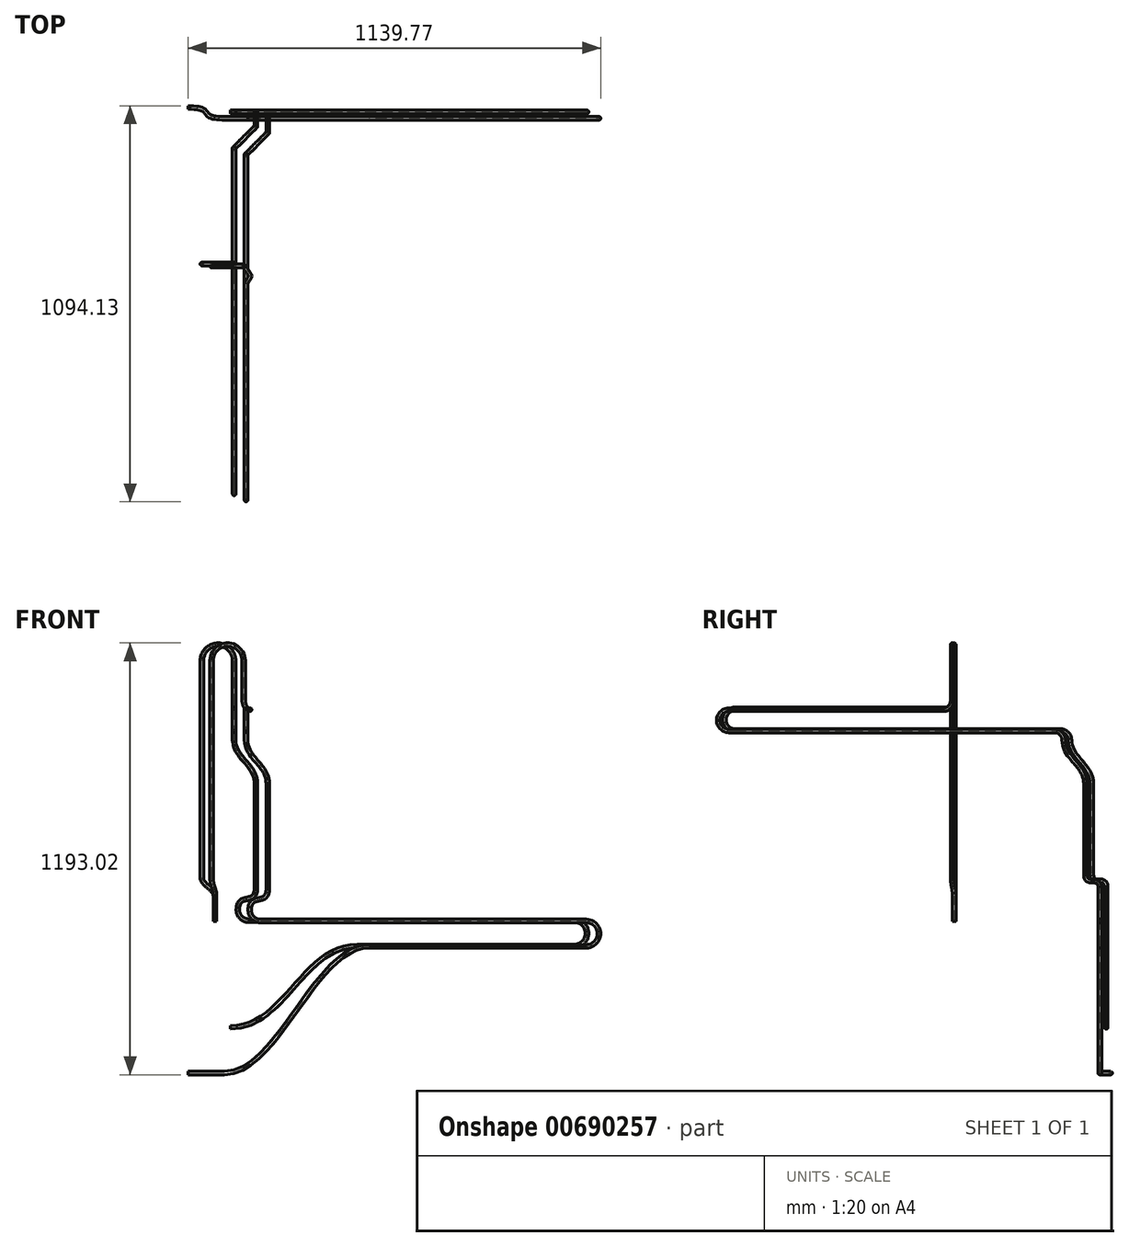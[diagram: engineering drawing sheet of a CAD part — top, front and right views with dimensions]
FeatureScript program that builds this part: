
annotation { "Feature Type Name" : "Feature", "Feature Type Description" : "" }
export const myFeature = defineFeature(function(context is Context, id is Id, definition is map)
    precondition{}
    {
        {
            var Q0;
            Q0=qCreatedBy(makeId("Top.planeOp"),FACE);
            var sketch = newSketch(context, id + "F0", { "sketchPlane" : qUnion([Q0])});
            skCircle(sketch, "E0", {"center": v(0, 0) * mm, "radius": 4.76 * mm});
            skCircle(sketch, "E1", {"center": v(0, 0) * mm, "radius": 3.17 * mm});
            skSolve(sketch);
        }
        {
            var Q0;
            Q0=qCreatedBy(makeId("Front.planeOp"),FACE);
            var sketch = newSketch(context, id + "F1", { "sketchPlane" : qUnion([Q0])});
            skLineSegment(sketch, "E2", {"start": v(0, 70) * mm, "end": v(0, 0) * mm});
            skSolve(sketch);
        }
        {
            var Q0;
            Q0=sQuery(id+"F1.wireOp",EDGE,"E2");
            cPlane(context, id + "F2", {"entities" : qUnion([Q0]), "cplaneType" : CPlaneType.LINE_ANGLE, "offset" : 25 * mm, "angle" : 120 * degree, "oppositeDirection" : true, "width" : 150 * mm, "height" : 150 * mm});
        }
        {
            var Q0;
            Q0=qCreatedBy(id+"F2.planeOp",FACE);
            var sketch = newSketch(context, id + "F3", { "sketchPlane" : qUnion([Q0])});
            skFitSpline(sketch, "E3", {"points": [v(0, 70) * mm, v(-5.5, 95) * mm, v(-11, 120) * mm], "startDerivative": vector(0, 60) * mm, "endDerivative": vector(0, 60) * mm});
            skLineSegment(sketch, "E4", {"start": v(-11, 110) * mm, "end": v(-11, 120) * mm, "construction": true});
            skLineSegment(sketch, "E5", {"start": v(0, 80) * mm, "end": v(0, 70) * mm, "construction": true});
            skLineSegment(sketch, "E6", {"start": v(0, 70) * mm, "end": v(-11, 120) * mm, "construction": true});
            skSolve(sketch);
        }
        {
            var Q0;
            Q0=qCreatedBy(makeId("Front.planeOp"),FACE);
            var Q1;
            Q1=sQuery(id+"F3.wireOp",VERTEX,"E3.2.internal");
            cPlane(context, id + "F4", {"entities" : qUnion([Q0, Q1]), "cplaneType" : CPlaneType.PLANE_POINT, "offset" : 25 * mm, "width" : 150 * mm, "height" : 150 * mm});
        }
        {
            var Q0;
            Q0=qCreatedBy(id+"F4.planeOp",FACE);
            var sketch = newSketch(context, id + "F5", { "sketchPlane" : qUnion([Q0])});
            skLineSegment(sketch, "E7", {"start": v(79.47, 612) * mm, "end": v(79.47, 720) * mm});
            skArc(sketch, "E8", {"start": v(79.47, 720) * mm, "mid": v(34.97, 764.5) * mm, "end": v(-9.53, 720) * mm});
            skLineSegment(sketch, "E9", {"start": v(-9.53, 120) * mm, "end": v(-9.53, 720) * mm});
            skSolve(sketch);
        }
        {
            var Q0;
            Q0=sQuery(id+"F5.wireOp",EDGE,"E7");
            cPlane(context, id + "F6", {"entities" : qUnion([Q0]), "cplaneType" : CPlaneType.LINE_ANGLE, "offset" : 25 * mm, "angle" : 35 * degree, "width" : 150 * mm, "height" : 150 * mm});
        }
        {
            var Q0;
            Q0=qCreatedBy(id+"F6.planeOp",FACE);
            var sketch = newSketch(context, id + "F7", { "sketchPlane" : qUnion([Q0])});
            skArc(sketch, "E10", {"start": v(-77.09, 585) * mm, "mid": v(-58, 592.9) * mm, "end": v(-50.09, 612) * mm});
            skSolve(sketch);
        }
        {
            var Q0;
            Q0=qCreatedBy(makeId("Top.planeOp"),FACE);
            var Q1;
            Q1=sQuery(id+"F7.wireOp",VERTEX,"E10.start");
            cPlane(context, id + "F8", {"entities" : qUnion([Q0, Q1]), "cplaneType" : CPlaneType.PLANE_POINT, "offset" : 25 * mm, "width" : 150 * mm, "height" : 150 * mm});
        }
        {
            var Q0;
            Q0=qCreatedBy(id+"F8.planeOp",FACE);
            var sketch = newSketch(context, id + "F9", { "sketchPlane" : qUnion([Q0])});
            skFitSpline(sketch, "E11", {"points": [v(94.96, -27.62) * mm, v(88.96, -47.62) * mm, v(85.96, -67.62) * mm], "startDerivative": vector(34.14, -48.76) * mm, "endDerivative": vector(0, -60.48) * mm});
            skLineSegment(sketch, "E12", {"start": v(100.7, -35.8) * mm, "end": v(94.96, -27.62) * mm, "construction": true});
            skLineSegment(sketch, "E13", {"start": v(85.96, -57.62) * mm, "end": v(85.96, -67.62) * mm, "construction": true});
            skSolve(sketch);
        }
        {
            var Q0;
            Q0=qCreatedBy(makeId("Right.planeOp"),FACE);
            var Q1;
            Q1=sQuery(id+"F9.wireOp",VERTEX,"E11.end");
            cPlane(context, id + "F10", {"entities" : qUnion([Q0, Q1]), "cplaneType" : CPlaneType.PLANE_POINT, "offset" : 25 * mm, "width" : 150 * mm, "height" : 150 * mm});
        }
        {
            var Q0;
            Q0=qCreatedBy(id+"F10.planeOp",FACE);
            var sketch = newSketch(context, id + "F11", { "sketchPlane" : qUnion([Q0])});
            skArc(sketch, "E14.MirrorCS", {"start": v(277.38, 526) * mm, "mid": v(295.06, 518.68) * mm, "end": v(302.38, 501) * mm});
            skLineSegment(sketch, "E15.MirrorCS", {"start": v(302.38, 501) * mm, "end": v(302.38, 516.1) * mm, "construction": true});
            skLineSegment(sketch, "E16.MirrorCS", {"start": v(-67.62, 585) * mm, "end": v(-622.62, 585) * mm});
            skArc(sketch, "E17.MirrorCS", {"start": v(-622.62, 526) * mm, "mid": v(-652.12, 555.5) * mm, "end": v(-622.62, 585) * mm});
            skLineSegment(sketch, "E18.MirrorCS", {"start": v(-622.62, 526) * mm, "end": v(277.38, 526) * mm});
            skSolve(sketch);
        }
        {
            var Q0;
            Q0=sQuery(id+"F11.wireOp",EDGE,"E15.MirrorCS");
            cPlane(context, id + "F12", {"entities" : qUnion([Q0]), "cplaneType" : CPlaneType.LINE_ANGLE, "offset" : 25 * mm, "angle" : 45 * degree, "oppositeDirection" : true, "width" : 150 * mm, "height" : 150 * mm});
        }
        {
            var Q0;
            Q0=qCreatedBy(id+"F12.planeOp",FACE);
            var sketch = newSketch(context, id + "F13", { "sketchPlane" : qUnion([Q0])});
            skFitSpline(sketch, "E19", {"points": [v(274.6, 501) * mm, v(317.1, 441) * mm, v(359.6, 381) * mm], "startDerivative": vector(0, -150) * mm, "endDerivative": vector(0, -150) * mm});
            skLineSegment(sketch, "E20", {"start": v(274.6, 476) * mm, "end": v(274.6, 501) * mm, "construction": true});
            skLineSegment(sketch, "E21", {"start": v(359.6, 406) * mm, "end": v(359.6, 381) * mm, "construction": true});
            skLineSegment(sketch, "E22", {"start": v(359.6, 381) * mm, "end": v(274.6, 501) * mm, "construction": true});
            skLineSegment(sketch, "E23", {"start": v(359.6, 381) * mm, "end": v(359.6, 131) * mm});
            skSolve(sketch);
        }
        {
            var Q0;
            Q0=qCreatedBy(makeId("Right.planeOp"),FACE);
            var Q1;
            Q1=sQuery(id+"F13.wireOp",VERTEX,"E23.end");
            cPlane(context, id + "F14", {"entities" : qUnion([Q0, Q1]), "cplaneType" : CPlaneType.PLANE_POINT, "offset" : 25 * mm, "width" : 150 * mm, "height" : 150 * mm});
        }
        {
            var Q0;
            Q0=qCreatedBy(id+"F14.planeOp",FACE);
            var sketch = newSketch(context, id + "F15", { "sketchPlane" : qUnion([Q0])});
            skFitSpline(sketch, "E24", {"points": [v(362.49, 131) * mm, v(382.49, 111) * mm, v(402.49, 91) * mm], "startDerivative": vector(0, -120) * mm, "endDerivative": vector(0, -120) * mm});
            skLineSegment(sketch, "E25", {"start": v(362.49, 131) * mm, "end": v(362.49, 111) * mm, "construction": true});
            skLineSegment(sketch, "E26", {"start": v(402.49, 111) * mm, "end": v(402.49, 91) * mm, "construction": true});
            skLineSegment(sketch, "E27", {"start": v(402.49, 91) * mm, "end": v(362.49, 131) * mm, "construction": true});
            skSolve(sketch);
        }
        {
            var Q0;
            Q0=sQuery(id+"F15.wireOp",VERTEX,"E24.end");
            var Q1;
            Q1=qCreatedBy(makeId("Front.planeOp"),FACE);
            cPlane(context, id + "F16", {"entities" : qUnion([Q0, Q1]), "cplaneType" : CPlaneType.PLANE_POINT, "offset" : 25 * mm, "width" : 150 * mm, "height" : 150 * mm});
        }
        {
            var Q0;
            Q0=qCreatedBy(id+"F16.planeOp",FACE);
            var sketch = newSketch(context, id + "F17", { "sketchPlane" : qUnion([Q0])});
            skFitSpline(sketch, "E28", {"points": [v(146.06, 91) * mm, v(121.06, 61) * mm, v(96.06, 31) * mm], "startDerivative": vector(0, -150) * mm, "endDerivative": vector(0, -150) * mm});
            skLineSegment(sketch, "E29", {"start": v(146.06, 91) * mm, "end": v(146.06, 66) * mm, "construction": true});
            skLineSegment(sketch, "E30", {"start": v(96.06, 56) * mm, "end": v(96.06, 31) * mm, "construction": true});
            skLineSegment(sketch, "E31", {"start": v(96.06, 31) * mm, "end": v(146.06, 91) * mm, "construction": true});
            skArc(sketch, "E32", {"start": v(96.06, 31) * mm, "mid": v(104.85, 9.79) * mm, "end": v(126.06, 1) * mm});
            skLineSegment(sketch, "E33", {"start": v(126.06, 1) * mm, "end": v(1026.06, 1) * mm});
            skArc(sketch, "E34", {"start": v(1026.06, -69) * mm, "mid": v(1061.06, -34) * mm, "end": v(1026.06, 1) * mm});
            skLineSegment(sketch, "E35", {"start": v(1026.06, -69) * mm, "end": v(426.06, -69) * mm});
            skFitSpline(sketch, "E36", {"points": [v(426.06, -69) * mm, v(226.06, -244) * mm, v(26.06, -419) * mm], "startDerivative": vector(-450, 0) * mm, "endDerivative": vector(-450, 0) * mm});
            skLineSegment(sketch, "E37", {"start": v(426.06, -69) * mm, "end": v(351.06, -69) * mm, "construction": true});
            skLineSegment(sketch, "E38", {"start": v(101.06, -419) * mm, "end": v(26.06, -419) * mm, "construction": true});
            skLineSegment(sketch, "E39", {"start": v(26.06, -419) * mm, "end": v(426.06, -69) * mm, "construction": true});
            skSolve(sketch);
        }
        {
            var Q0;
            Q0=sQuery(id+"F17.wireOp",VERTEX,"E36.end");
            var Q1;
            Q1=qCreatedBy(makeId("Top.planeOp"),FACE);
            cPlane(context, id + "F18", {"entities" : qUnion([Q0, Q1]), "cplaneType" : CPlaneType.PLANE_POINT, "offset" : 25 * mm, "width" : 150 * mm, "height" : 150 * mm});
        }
        {
            var Q0;
            Q0=qCreatedBy(id+"F18.planeOp",FACE);
            var sketch = newSketch(context, id + "F19", { "sketchPlane" : qUnion([Q0])});
            skFitSpline(sketch, "E40", {"points": [v(26.06, 402.49) * mm, v(-23.94, 417.49) * mm, v(-73.94, 432.49) * mm], "startDerivative": vector(-240, 0) * mm, "endDerivative": vector(-240, 0) * mm});
            skLineSegment(sketch, "E41", {"start": v(-13.94, 402.49) * mm, "end": v(26.06, 402.49) * mm, "construction": true});
            skLineSegment(sketch, "E42", {"start": v(-33.94, 432.49) * mm, "end": v(-73.94, 432.49) * mm, "construction": true});
            skLineSegment(sketch, "E43", {"start": v(-73.94, 432.49) * mm, "end": v(26.06, 402.49) * mm, "construction": true});
            skSolve(sketch);
        }
        {
            var Q0;
            Q0=qSketchRegion(id+"F0",true);
            var Q1;
            Q1=qConstructionFilter(qBodyType(qCreatedBy(id+"F1",EDGE),BodyType.WIRE),ConstructionObject.NO);
            var Q2;
            Q2=qConstructionFilter(qBodyType(qCreatedBy(id+"F3",EDGE),BodyType.WIRE),ConstructionObject.NO);
            var Q3;
            Q3=qConstructionFilter(qBodyType(qCreatedBy(id+"F5",EDGE),BodyType.WIRE),ConstructionObject.NO);
            var Q4;
            Q4=qConstructionFilter(qBodyType(qCreatedBy(id+"F11",EDGE),BodyType.WIRE),ConstructionObject.NO);
            var Q5;
            Q5=qConstructionFilter(qBodyType(qCreatedBy(id+"F13",EDGE),BodyType.WIRE),ConstructionObject.NO);
            var Q6;
            Q6=qConstructionFilter(qBodyType(qCreatedBy(id+"F15",EDGE),BodyType.WIRE),ConstructionObject.NO);
            var Q7;
            Q7=qConstructionFilter(qBodyType(qCreatedBy(id+"F17",EDGE),BodyType.WIRE),ConstructionObject.NO);
            var Q8;
            Q8=qConstructionFilter(qBodyType(qCreatedBy(id+"F19",EDGE),BodyType.WIRE),ConstructionObject.NO);
            var Q9;
            Q9=qConstructionFilter(qBodyType(qCreatedBy(id+"F7",EDGE),BodyType.WIRE),ConstructionObject.NO);
            var Q10;
            Q10=qConstructionFilter(qBodyType(qCreatedBy(id+"F9",EDGE),BodyType.WIRE),ConstructionObject.NO);
            sweep(context, id + "F20", {"profiles" : qUnion([Q0]), "path" : qUnion([Q1, Q2, Q3, Q4, Q5, Q6, Q7, Q8, Q9, Q10])});
        }
        {
            var Q0;
            Q0=qCreatedBy(makeId("Front.planeOp"),FACE);
            var sketch = newSketch(context, id + "F21", { "sketchPlane" : qUnion([Q0])});
            skLineSegment(sketch, "E44", {"start": v(53, 612) * mm, "end": v(53, 720) * mm});
            skArc(sketch, "E45", {"start": v(53, 720) * mm, "mid": v(8.5, 764.5) * mm, "end": v(-36, 720) * mm});
            skLineSegment(sketch, "E46", {"start": v(0, 70) * mm, "end": v(0, 0) * mm});
            skFitSpline(sketch, "E47", {"points": [v(0, 70) * mm, v(-18, 95) * mm, v(-36, 120) * mm], "startDerivative": vector(0, 60) * mm, "endDerivative": vector(0, 60) * mm});
            skLineSegment(sketch, "E48", {"start": v(-36, 110) * mm, "end": v(-36, 120) * mm, "construction": true});
            skLineSegment(sketch, "E49", {"start": v(0, 80) * mm, "end": v(0, 70) * mm, "construction": true});
            skLineSegment(sketch, "E50", {"start": v(0, 70) * mm, "end": v(-36, 120) * mm, "construction": true});
            skLineSegment(sketch, "E51", {"start": v(-36, 120) * mm, "end": v(-36, 720) * mm});
            skSolve(sketch);
        }
        {
            var Q0;
            Q0=qCreatedBy(makeId("Right.planeOp"),FACE);
            var Q1;
            Q1=sQuery(id+"F21.wireOp",VERTEX,"E44.start");
            cPlane(context, id + "F22", {"entities" : qUnion([Q0, Q1]), "cplaneType" : CPlaneType.PLANE_POINT, "offset" : 25 * mm, "width" : 150 * mm, "height" : 150 * mm});
        }
        {
            var Q0;
            Q0=qCreatedBy(id+"F22.planeOp",FACE);
            var sketch = newSketch(context, id + "F23", { "sketchPlane" : qUnion([Q0])});
            skArc(sketch, "E52.MirrorCS", {"start": v(0, 612) * mm, "mid": v(-7.32, 594.32) * mm, "end": v(-25, 587) * mm});
            skArc(sketch, "E53.MirrorCS", {"start": v(295, 527) * mm, "mid": v(312.68, 519.68) * mm, "end": v(320, 502) * mm});
            skLineSegment(sketch, "E54.MirrorCS", {"start": v(320, 502) * mm, "end": v(320, 517.1) * mm, "construction": true});
            skLineSegment(sketch, "E55.MirrorCS", {"start": v(-25, 587) * mm, "end": v(-605, 587) * mm});
            skArc(sketch, "E56.MirrorCS", {"start": v(-605, 527) * mm, "mid": v(-635, 557) * mm, "end": v(-605, 587) * mm});
            skLineSegment(sketch, "E57.MirrorCS", {"start": v(-605, 527) * mm, "end": v(295, 527) * mm});
            skSolve(sketch);
        }
        {
            var Q0;
            Q0=sQuery(id+"F23.wireOp",EDGE,"E54.MirrorCS");
            cPlane(context, id + "F24", {"entities" : qUnion([Q0]), "cplaneType" : CPlaneType.LINE_ANGLE, "offset" : 25 * mm, "angle" : 45 * degree, "oppositeDirection" : true, "width" : 150 * mm, "height" : 150 * mm});
        }
        {
            var Q0;
            Q0=qCreatedBy(id+"F24.planeOp",FACE);
            var sketch = newSketch(context, id + "F25", { "sketchPlane" : qUnion([Q0])});
            skFitSpline(sketch, "E58", {"points": [v(263.75, 502) * mm, v(306.25, 442) * mm, v(348.75, 382) * mm], "startDerivative": vector(0, -150) * mm, "endDerivative": vector(0, -150) * mm});
            skLineSegment(sketch, "E59", {"start": v(263.75, 477) * mm, "end": v(263.75, 502) * mm, "construction": true});
            skLineSegment(sketch, "E60", {"start": v(348.75, 407) * mm, "end": v(348.75, 382) * mm, "construction": true});
            skLineSegment(sketch, "E61", {"start": v(348.75, 382) * mm, "end": v(263.75, 502) * mm, "construction": true});
            skLineSegment(sketch, "E62", {"start": v(348.75, 382) * mm, "end": v(348.75, 132) * mm});
            skSolve(sketch);
        }
        {
            var Q0;
            Q0=qCreatedBy(makeId("Right.planeOp"),FACE);
            var Q1;
            Q1=sQuery(id+"F25.wireOp",VERTEX,"E62.end");
            cPlane(context, id + "F26", {"entities" : qUnion([Q0, Q1]), "cplaneType" : CPlaneType.PLANE_POINT, "offset" : 25 * mm, "width" : 150 * mm, "height" : 150 * mm});
        }
        {
            var Q0;
            Q0=qCreatedBy(id+"F26.planeOp",FACE);
            var sketch = newSketch(context, id + "F27", { "sketchPlane" : qUnion([Q0])});
            skFitSpline(sketch, "E63", {"points": [v(380.1, 132) * mm, v(400.1, 112) * mm, v(420.1, 92) * mm], "startDerivative": vector(0, -120) * mm, "endDerivative": vector(0, -120) * mm});
            skLineSegment(sketch, "E64", {"start": v(380.1, 132) * mm, "end": v(380.1, 112) * mm, "construction": true});
            skLineSegment(sketch, "E65", {"start": v(420.1, 112) * mm, "end": v(420.1, 92) * mm, "construction": true});
            skLineSegment(sketch, "E66", {"start": v(420.1, 92) * mm, "end": v(380.1, 132) * mm, "construction": true});
            skSolve(sketch);
        }
        {
            var Q0;
            Q0=qCreatedBy(makeId("Front.planeOp"),FACE);
            var Q1;
            Q1=sQuery(id+"F27.wireOp",VERTEX,"E63.end");
            cPlane(context, id + "F28", {"entities" : qUnion([Q0, Q1]), "cplaneType" : CPlaneType.PLANE_POINT, "offset" : 25 * mm, "width" : 150 * mm, "height" : 150 * mm});
        }
        {
            var Q0;
            Q0=qCreatedBy(id+"F28.planeOp",FACE);
            var sketch = newSketch(context, id + "F29", { "sketchPlane" : qUnion([Q0])});
            skFitSpline(sketch, "E67", {"points": [v(113.1, 92) * mm, v(88.1, 62) * mm, v(63.1, 32) * mm], "startDerivative": vector(0, -150) * mm, "endDerivative": vector(0, -150) * mm});
            skLineSegment(sketch, "E68", {"start": v(113.1, 92) * mm, "end": v(113.1, 67) * mm, "construction": true});
            skLineSegment(sketch, "E69", {"start": v(63.1, 57) * mm, "end": v(63.1, 32) * mm, "construction": true});
            skLineSegment(sketch, "E70", {"start": v(63.1, 32) * mm, "end": v(113.1, 92) * mm, "construction": true});
            skArc(sketch, "E71", {"start": v(63.1, 32) * mm, "mid": v(71.9, 10.79) * mm, "end": v(93.1, 2) * mm});
            skLineSegment(sketch, "E72", {"start": v(93.1, 2) * mm, "end": v(993.1, 2) * mm});
            skArc(sketch, "E73", {"start": v(993.1, -68) * mm, "mid": v(1028.1, -33) * mm, "end": v(993.1, 2) * mm});
            skLineSegment(sketch, "E74", {"start": v(993.1, -68) * mm, "end": v(393.1, -68) * mm});
            skFitSpline(sketch, "E75", {"points": [v(393.1, -68) * mm, v(218.1, -180.5) * mm, v(43.1, -293) * mm], "startDerivative": vector(-450, 0) * mm, "endDerivative": vector(-450, 0) * mm});
            skLineSegment(sketch, "E76", {"start": v(393.1, -68) * mm, "end": v(318.1, -68) * mm, "construction": true});
            skLineSegment(sketch, "E77", {"start": v(118.1, -293) * mm, "end": v(43.1, -293) * mm, "construction": true});
            skLineSegment(sketch, "E78", {"start": v(43.1, -293) * mm, "end": v(393.1, -68) * mm, "construction": true});
            skSolve(sketch);
        }
        {
            var Q0;
            Q0=qSketchRegion(id+"F0",true);
            var Q1;
            Q1=qConstructionFilter(qBodyType(qCreatedBy(id+"F21",EDGE),BodyType.WIRE),ConstructionObject.NO);
            var Q2;
            Q2=qConstructionFilter(qBodyType(qCreatedBy(id+"F23",EDGE),BodyType.WIRE),ConstructionObject.NO);
            var Q3;
            Q3=qConstructionFilter(qBodyType(qCreatedBy(id+"F25",EDGE),BodyType.WIRE),ConstructionObject.NO);
            var Q4;
            Q4=qConstructionFilter(qBodyType(qCreatedBy(id+"F27",EDGE),BodyType.WIRE),ConstructionObject.NO);
            var Q5;
            Q5=qConstructionFilter(qBodyType(qCreatedBy(id+"F29",EDGE),BodyType.WIRE),ConstructionObject.NO);
            sweep(context, id + "F30", {"profiles" : qUnion([Q0]), "path" : qUnion([Q1, Q2, Q3, Q4, Q5])});
        }
    });
